SOLIDWORKS PART (.sldprt)
format: sldprt  version: not decoded by parser v0  size: 140,288 bytes
history: native  units: mm
features: sketch x5, cut_extrude x4, plane x3, material x1, extrude x1 (+10 scaffold rows collapsed)
feature tree (24):
  scaffold x10  (default folders/planes/origin — collapsed)
  material  "Matériau <non spécifié>"
  plane  "Plan de face"
  plane  "Plan de dessus"
  plane  "Plan de droite"
  sketch  "Esquisse1"  dims[D1=~539.943801mm]
  extrude  "Boss.-Extru.1"  Depth=22mm
  sketch  "Esquisse2"
  cut_extrude  "Enlèv. mat.-Extru.1"  [1 undecoded]
  sketch  "Esquisse3"
  cut_extrude  "Enlèv. mat.-Extru.2"  Depth=8mm
  sketch  "Esquisse4"  dims[D1=~12.242968mm]
  cut_extrude  "Enlèv. mat.-Extru.3"  Depth=5mm
  sketch  "Esquisse6"
  cut_extrude  "Enlèv. mat.-Extru.4"  [1 undecoded]
decode coverage: 5 of 10 modeling features carry decoded parameters
note: ~ marks probable driven/reference dimensions
note: 2 parameter values undecoded
note: suppression state not decoded; provenance and decode notes live in map.json
